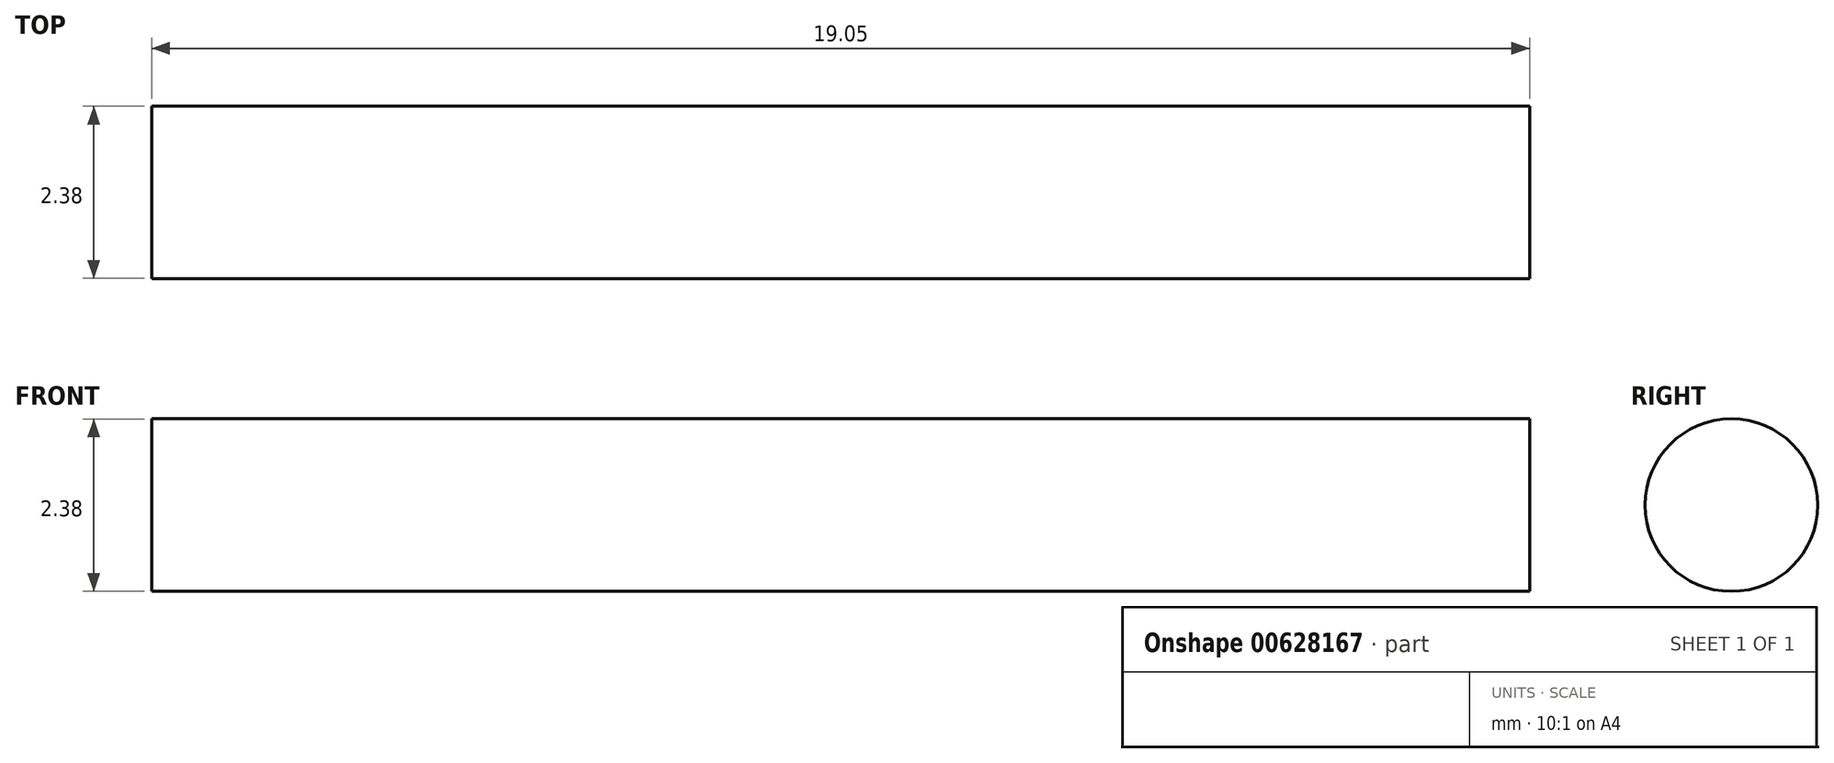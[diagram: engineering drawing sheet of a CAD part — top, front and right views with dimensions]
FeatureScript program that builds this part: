
annotation { "Feature Type Name" : "Feature", "Feature Type Description" : "" }
export const myFeature = defineFeature(function(context is Context, id is Id, definition is map)
    precondition{}
    {
        {
            var Q0;
            Q0=qCreatedBy(makeId("Right.planeOp"),FACE);
            var sketch = newSketch(context, id + "F0", { "sketchPlane" : qUnion([Q0])});
            skCircle(sketch, "E0", {"center": v(0, 0) * mm, "radius": 1.2 * mm});
            skSolve(sketch);
        }
        {
            var Q0;
            Q0 = qSketchRegion(id + "F0", true);
            extrude(context, id + "F1", {"entities" : qUnion([Q0]), "depth" : 19.05 * mm, "offsetDistance" : 25.4 * mm});
        }
    });
